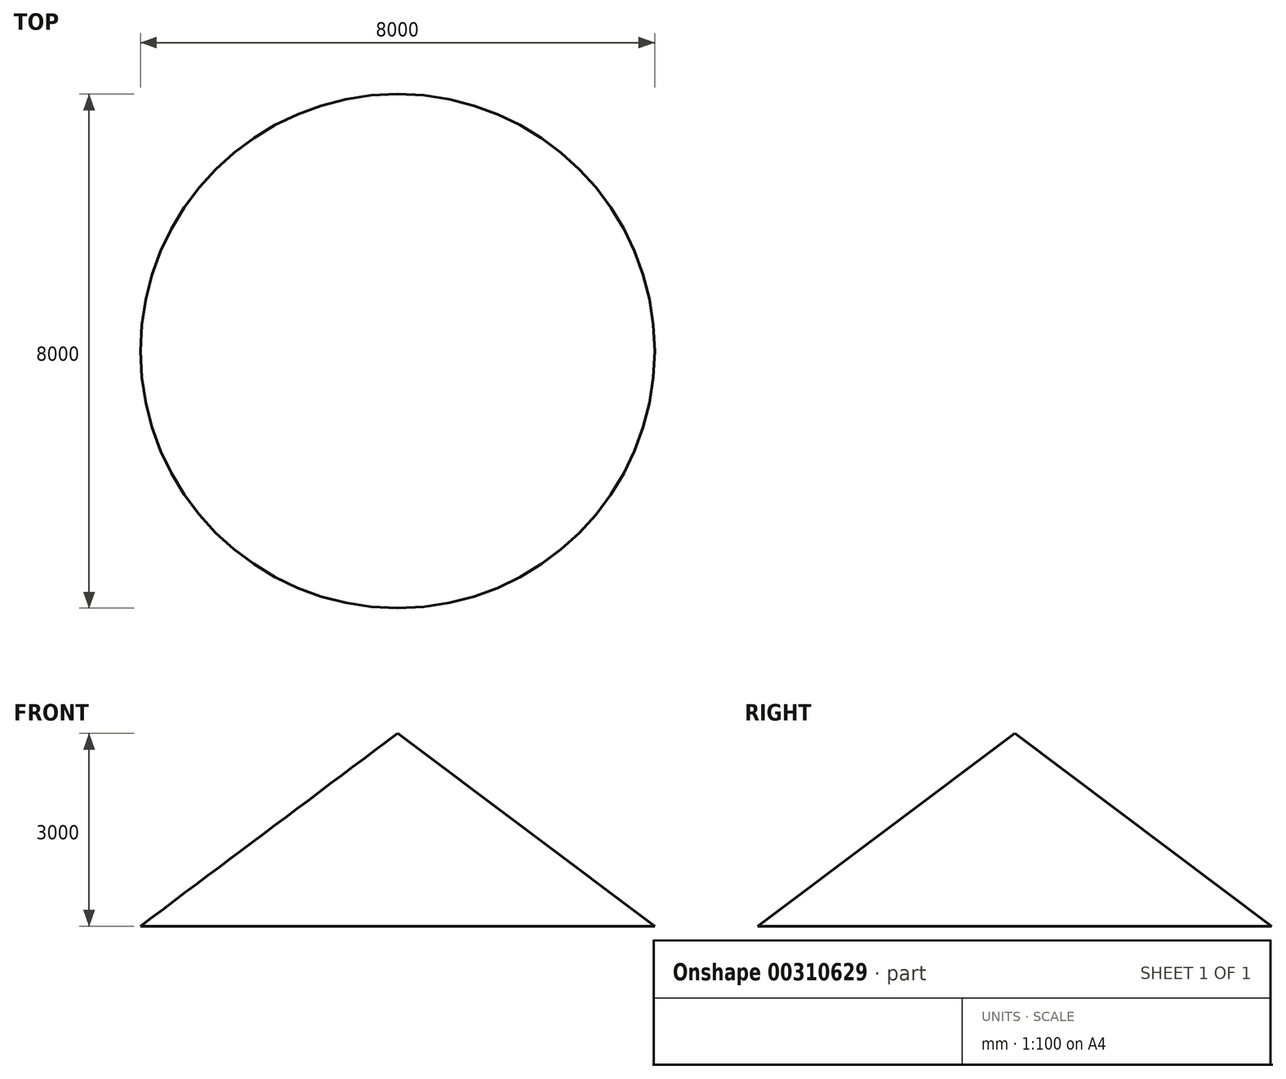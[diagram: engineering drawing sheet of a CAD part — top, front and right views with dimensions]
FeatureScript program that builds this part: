
annotation { "Feature Type Name" : "Feature", "Feature Type Description" : "" }
export const myFeature = defineFeature(function(context is Context, id is Id, definition is map)
    precondition{}
    {
        {
            var Q0;
            Q0=qCreatedBy(makeId("Front.planeOp"),FACE);
            var sketch = newSketch(context, id + "F0", { "sketchPlane" : qUnion([Q0])});
            skLineSegment(sketch, "E0", {"start": v(0, 0) * mm, "end": v(0, 3000) * mm, "construction": true});
            skLineSegment(sketch, "E1", {"start": v(0, 3000) * mm, "end": v(4000, 0) * mm});
            skLineSegment(sketch, "E2", {"start": v(4000, 0) * mm, "end": v(0, 0) * mm});
            skSolve(sketch);
        }
        {
            var Q0;
            Q0=sQuery(id+"F0.wireOp",EDGE,"E1");
            var Q1;
            Q1=sQuery(id+"F0.wireOp",EDGE,"E2");
            var Q2;
            Q2=sQuery(id+"F0.wireOp",EDGE,"E0");
            revolve(context, id + "F1", {"bodyType" : ToolBodyType.SURFACE, "surfaceEntities" : qUnion([Q0, Q1]), "axis" : qUnion([Q2]), "revolveType" : RevolveType.FULL});
        }
    });
